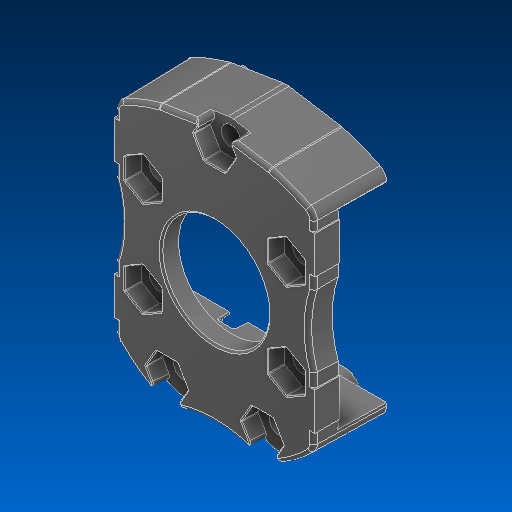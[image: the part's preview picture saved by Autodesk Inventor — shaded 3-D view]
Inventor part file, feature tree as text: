
AUTODESK INVENTOR PART (.ipt)
format: ipt  version: 2022.2 (Build 262287000, 287)  size: 2,529,280 bytes
history: native  units: in
note: dims shown in document units (in); Inventor stores cm internally (conversion verified against a paired STEP export)
features: chamfer x1
ambient origin geometry x8: Origin, YZ Plane, XZ Plane, XY Plane, X Axis, Y Axis, Z Axis, Center Point
bodies: Solid1 (feature_tree)
feature tree (1):
  chamfer  "Chamfer2"  [1 undecoded]
note: 1 required parameter value undecoded (feature->parameter linkage not recoverable at this tier; creation-order binding heuristic only, values carry confidence <= 0.55)
